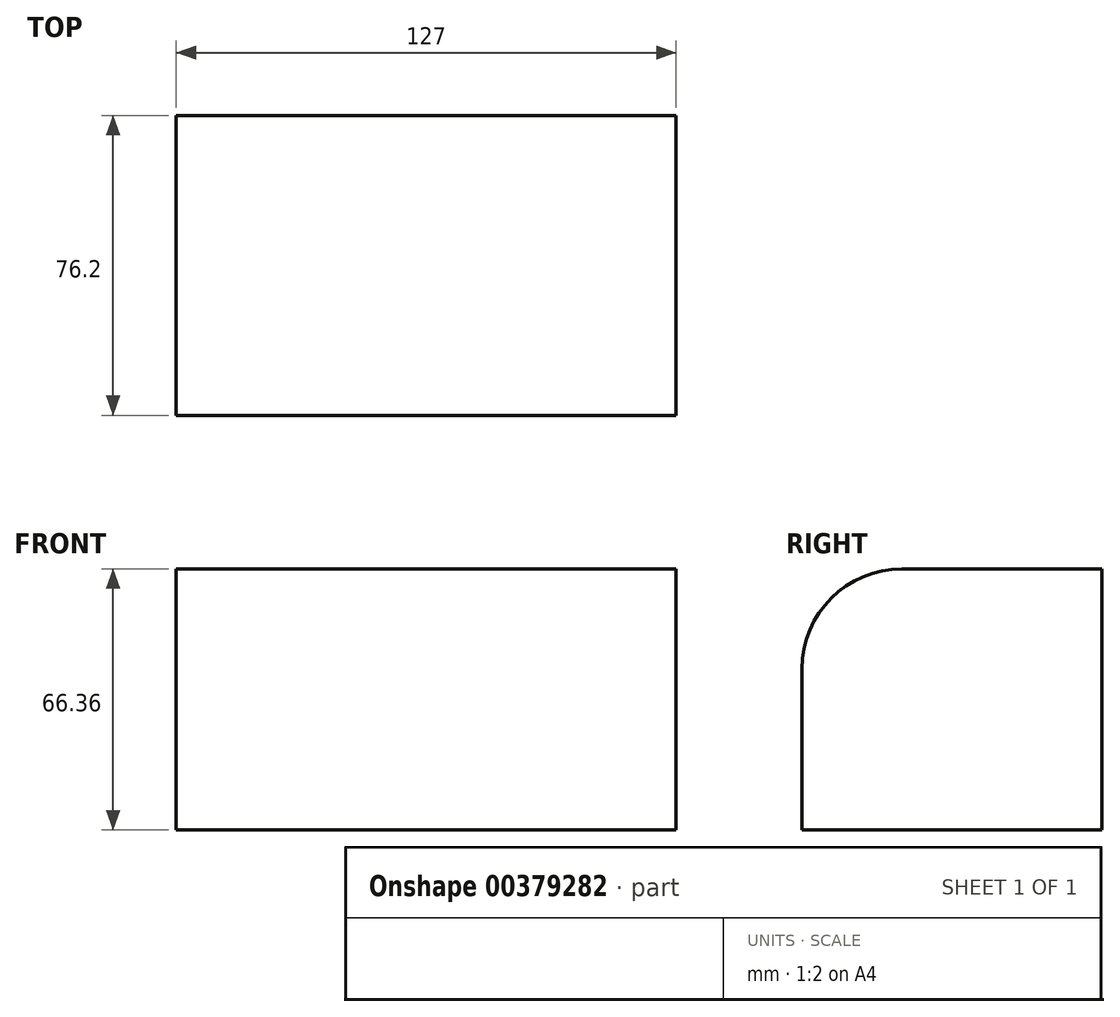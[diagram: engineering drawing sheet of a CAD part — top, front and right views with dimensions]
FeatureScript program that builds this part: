
annotation { "Feature Type Name" : "Feature", "Feature Type Description" : "" }
export const myFeature = defineFeature(function(context is Context, id is Id, definition is map)
    precondition{}
    {
        {
            var Q0;
            Q0=qCreatedBy(makeId("Front.planeOp"),FACE);
            var sketch = newSketch(context, id + "F0", { "sketchPlane" : qUnion([Q0])});
            skLineSegment(sketch, "E0.bottom", {"start": v(-63.5, 33.18) * mm, "end": v(63.5, 33.18) * mm});
            skLineSegment(sketch, "E0.top", {"start": v(-63.5, -33.18) * mm, "end": v(63.5, -33.18) * mm});
            skLineSegment(sketch, "E0.left", {"start": v(-63.5, 33.18) * mm, "end": v(-63.5, -33.18) * mm});
            skLineSegment(sketch, "E0.right", {"start": v(63.5, 33.18) * mm, "end": v(63.5, -33.18) * mm});
            skPoint(sketch, "E0.middle", {"position": v(0, 0) * mm});
            skSolve(sketch);
        }
        {
            var Q0;
            Q0=makeQuery(id+"F0.imprint","IMPRINT",FACE,{"disambiguationData":[TD([[makeQuery(id+"F0.imprint","IMPRINT",EDGE,{"derivedFrom":sQuery(id+"F0.wireOp",EDGE,"E0.bottom")}),-1.0]])]});
            extrude(context, id + "F1", {"entities" : qUnion([Q0]), "depth" : 76.2 * mm});
        }
        {
            var Q0;
            Q0=makeQuery(id+"F1.opExtrude","CAP_EDGE",EDGE,{"disambiguationData":[OSD([sQuery(id+"F0.wireOp",EDGE,"E0.bottom")])],"isStart":false});
            fillet(context, id + "F2", {"entities" : qUnion([Q0]), "radius" : 25.4 * mm, "tangentPropagation" : true, "allowEdgeOverflow" : false});
        }
    });
